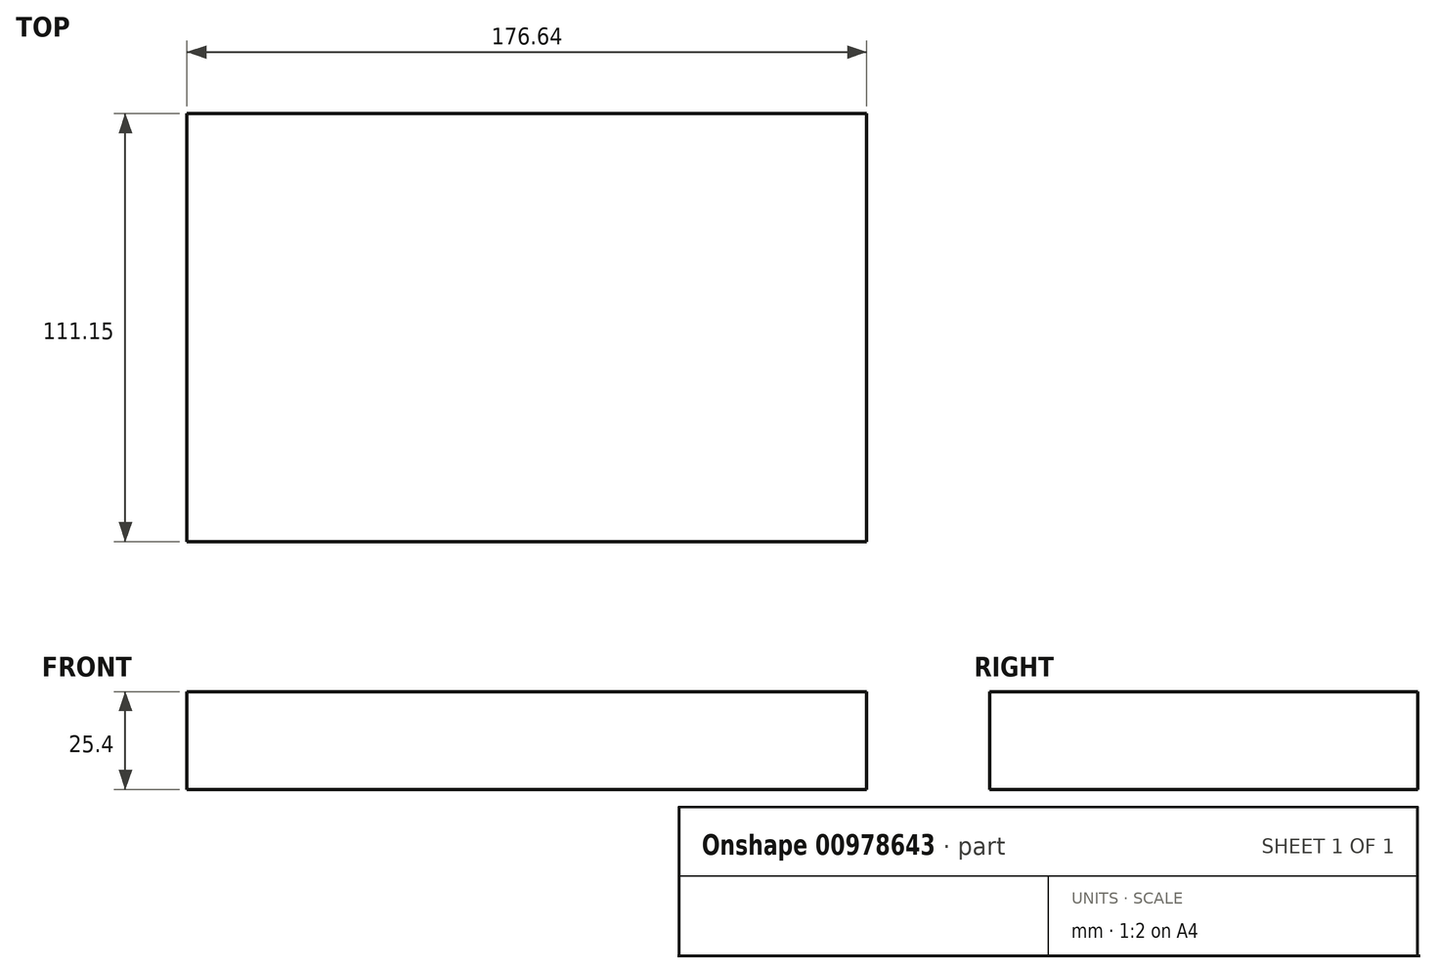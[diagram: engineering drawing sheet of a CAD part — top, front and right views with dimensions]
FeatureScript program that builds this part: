
annotation { "Feature Type Name" : "Feature", "Feature Type Description" : "" }
export const myFeature = defineFeature(function(context is Context, id is Id, definition is map)
    precondition{}
    {
        {
            var Q0;
            Q0=qCreatedBy(makeId("Top.planeOp"),FACE);
            var sketch = newSketch(context, id + "F0", { "sketchPlane" : qUnion([Q0])});
            skLineSegment(sketch, "E0.bottom", {"start": v(183.42, -126.52) * mm, "end": v(6.78, -126.52) * mm});
            skLineSegment(sketch, "E0.top", {"start": v(183.42, -15.37) * mm, "end": v(6.78, -15.37) * mm});
            skLineSegment(sketch, "E0.left", {"start": v(183.42, -126.52) * mm, "end": v(183.42, -15.37) * mm});
            skLineSegment(sketch, "E0.right", {"start": v(6.78, -126.52) * mm, "end": v(6.78, -15.37) * mm});
            skPoint(sketch, "E0.middle", {"position": v(95.1, -70.94) * mm});
            skSolve(sketch);
        }
        {
            var Q0;
            Q0 = qSketchRegion(id + "F0", true);
            extrude(context, id + "F1", {"entities" : qUnion([Q0]), "depth" : 25.4 * mm, "offsetDistance" : 25.4 * mm});
        }
    });
